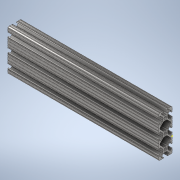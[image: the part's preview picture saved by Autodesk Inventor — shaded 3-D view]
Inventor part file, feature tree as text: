
AUTODESK INVENTOR PART (.ipt)
format: ipt  version: 2020 (Build 240168000, 168)  size: 378,368 bytes
history: native  units: in
note: dims shown in document units (in); Inventor stores cm internally (conversion verified against a paired STEP export)
features: sketch x2, extrude x1
ambient origin geometry x8: Origin, YZ Plane, XZ Plane, XY Plane, X Axis, Y Axis, Z Axis, Center Point
bodies: Solid1 (feature_tree)
feature tree (3):
  extrude  "Extrusion1"  [1 undecoded]
  sketch  "Sketch2"
  sketch  "Sketch1"  dims[d0=11.0in d1=0.0in]
note: 1 required parameter value undecoded (feature->parameter linkage not recoverable at this tier; creation-order binding heuristic only, values carry confidence <= 0.55)
